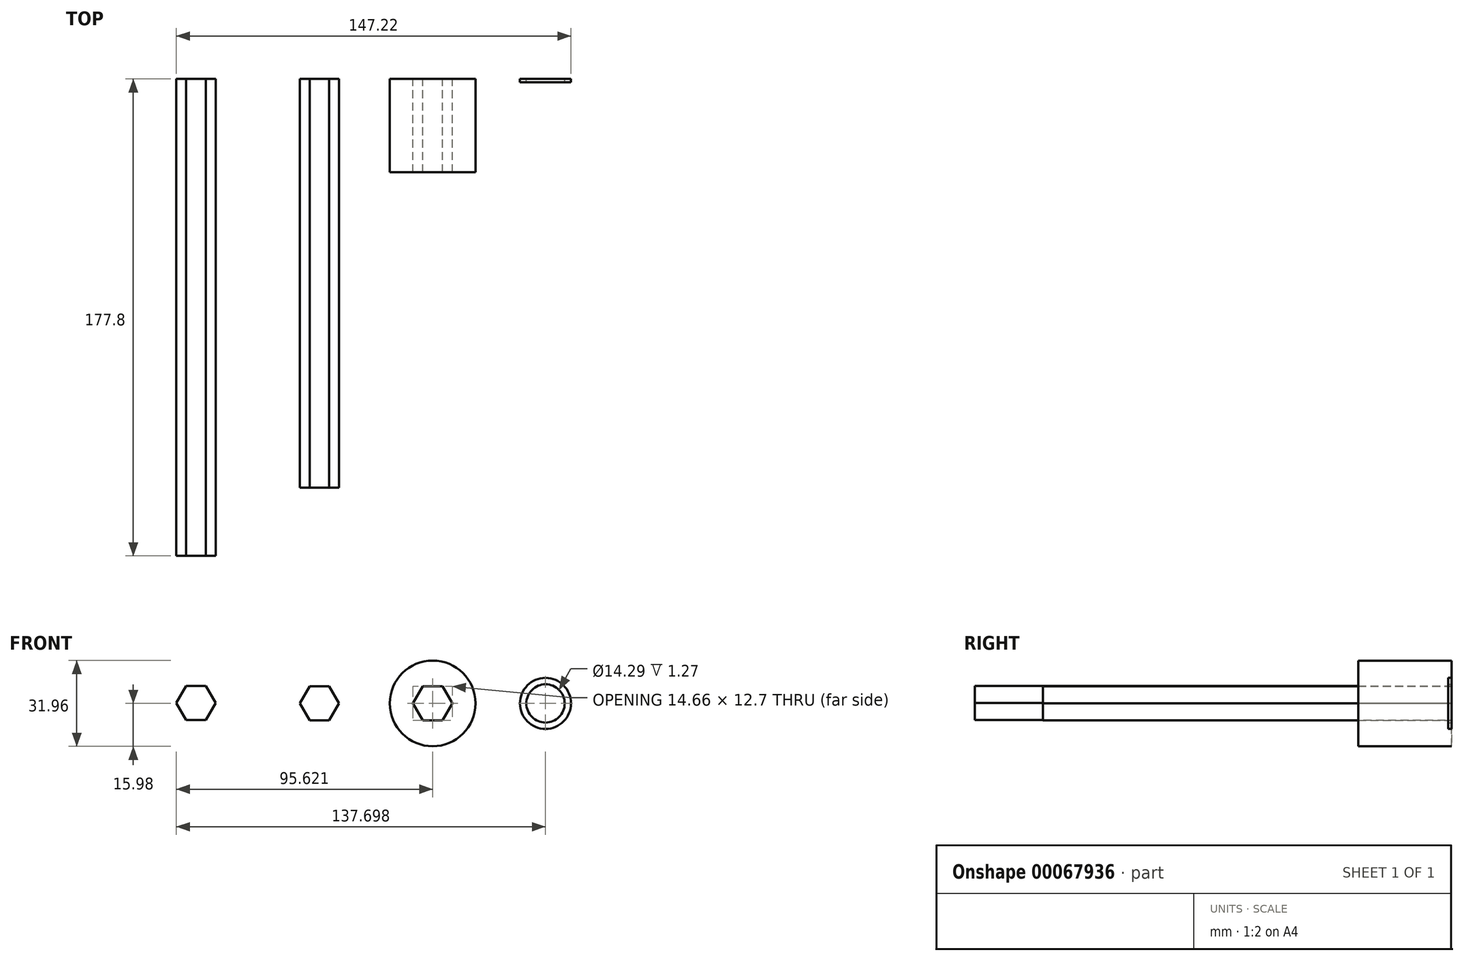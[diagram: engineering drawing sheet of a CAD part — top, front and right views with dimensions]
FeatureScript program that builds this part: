
annotation { "Feature Type Name" : "Feature", "Feature Type Description" : "" }
export const myFeature = defineFeature(function(context is Context, id is Id, definition is map)
    precondition{}
    {
        {
            var Q0;
            Q0=qCreatedBy(makeId("Front.planeOp"),FACE);
            var sketch = newSketch(context, id + "F0", { "sketchPlane" : qUnion([Q0])});
            skCircle(sketch, "E0.cCircle", {"center": v(0, 0) * mm, "radius": 6.35 * mm, "construction": true});
            skLineSegment(sketch, "E0.0", {"start": v(3.65, 6.36) * mm, "end": v(7.33, 0.02) * mm});
            skLineSegment(sketch, "E0.1", {"start": v(7.33, 0.02) * mm, "end": v(3.68, -6.34) * mm});
            skLineSegment(sketch, "E0.2", {"start": v(3.68, -6.34) * mm, "end": v(-3.65, -6.36) * mm});
            skLineSegment(sketch, "E0.3", {"start": v(-3.65, -6.36) * mm, "end": v(-7.33, -0.02) * mm});
            skLineSegment(sketch, "E0.4", {"start": v(-7.33, -0.02) * mm, "end": v(-3.68, 6.34) * mm});
            skLineSegment(sketch, "E0.5", {"start": v(-3.68, 6.34) * mm, "end": v(3.65, 6.36) * mm});
            skPoint(sketch, "E0.0.midPoint", {"position": v(5.5, 3.19) * mm});
            skCircle(sketch, "E1.cCircle", {"center": v(-46.05, 0.17) * mm, "radius": 6.35 * mm, "construction": true});
            skLineSegment(sketch, "E1.0", {"start": v(-42.4, 6.52) * mm, "end": v(-38.72, 0.18) * mm});
            skLineSegment(sketch, "E1.1", {"start": v(-38.72, 0.18) * mm, "end": v(-42.37, -6.18) * mm});
            skLineSegment(sketch, "E1.2", {"start": v(-42.37, -6.18) * mm, "end": v(-49.7, -6.2) * mm});
            skLineSegment(sketch, "E1.3", {"start": v(-49.7, -6.2) * mm, "end": v(-53.38, 0.15) * mm});
            skLineSegment(sketch, "E1.4", {"start": v(-53.38, 0.15) * mm, "end": v(-49.73, 6.5) * mm});
            skLineSegment(sketch, "E1.5", {"start": v(-49.73, 6.5) * mm, "end": v(-42.4, 6.52) * mm});
            skPoint(sketch, "E1.0.midPoint", {"position": v(-40.56, 3.35) * mm});
            skSolve(sketch);
        }
        {
            var Q0;
            Q0=makeQuery(id+"F0.imprint","IMPRINT",FACE,{"disambiguationData":[TD([[makeQuery(id+"F0.imprint","IMPRINT",EDGE,{"derivedFrom":sQuery(id+"F0.wireOp",EDGE,"E0.0")}),-1.0]])]});
            extrude(context, id + "F1", {"entities" : qUnion([Q0]), "depth" : 152.4 * mm});
        }
        {
            var Q0;
            Q0=makeQuery(id+"F0.imprint","IMPRINT",FACE,{"disambiguationData":[TD([[makeQuery(id+"F0.imprint","IMPRINT",EDGE,{"derivedFrom":sQuery(id+"F0.wireOp",EDGE,"E1.0")}),-1.0]])]});
            extrude(context, id + "F2", {"entities" : qUnion([Q0]), "depth" : 177.8 * mm});
        }
        {
            var Q0;
            Q0=qCreatedBy(makeId("Front.planeOp"),FACE);
            var sketch = newSketch(context, id + "F3", { "sketchPlane" : qUnion([Q0])});
            skCircle(sketch, "E2.cCircle", {"center": v(42.24, 0) * mm, "radius": 6.35 * mm, "construction": true});
            skLineSegment(sketch, "E2.0", {"start": v(38.58, 6.35) * mm, "end": v(45.9, 6.35) * mm});
            skLineSegment(sketch, "E2.1", {"start": v(45.9, 6.35) * mm, "end": v(49.57, 0) * mm});
            skLineSegment(sketch, "E2.2", {"start": v(49.57, 0) * mm, "end": v(45.9, -6.35) * mm});
            skLineSegment(sketch, "E2.3", {"start": v(45.9, -6.35) * mm, "end": v(38.58, -6.35) * mm});
            skLineSegment(sketch, "E2.4", {"start": v(38.58, -6.35) * mm, "end": v(34.9, 0) * mm});
            skLineSegment(sketch, "E2.5", {"start": v(34.9, 0) * mm, "end": v(38.58, 6.35) * mm});
            skPoint(sketch, "E2.0.midPoint", {"position": v(42.24, 6.35) * mm});
            skCircle(sketch, "E3", {"center": v(42.24, 0) * mm, "radius": 15.98 * mm});
            skSolve(sketch);
        }
        {
            var Q0;
            Q0 = qSketchRegion(id + "F3", true);
            extrude(context, id + "F4", {"entities" : qUnion([Q0]), "depth" : 34.8 * mm});
        }
        {
            var Q0;
            Q0=qCreatedBy(makeId("Front.planeOp"),FACE);
            var sketch = newSketch(context, id + "F5", { "sketchPlane" : qUnion([Q0])});
            skCircle(sketch, "E4", {"center": v(84.32, 0) * mm, "radius": 7.14 * mm});
            skCircle(sketch, "E5", {"center": v(84.32, 0) * mm, "radius": 9.53 * mm});
            skSolve(sketch);
        }
        {
            var Q0;
            Q0 = qSketchRegion(id + "F5", true);
            extrude(context, id + "F6", {"entities" : qUnion([Q0]), "depth" : 1.27 * mm});
        }
    });
